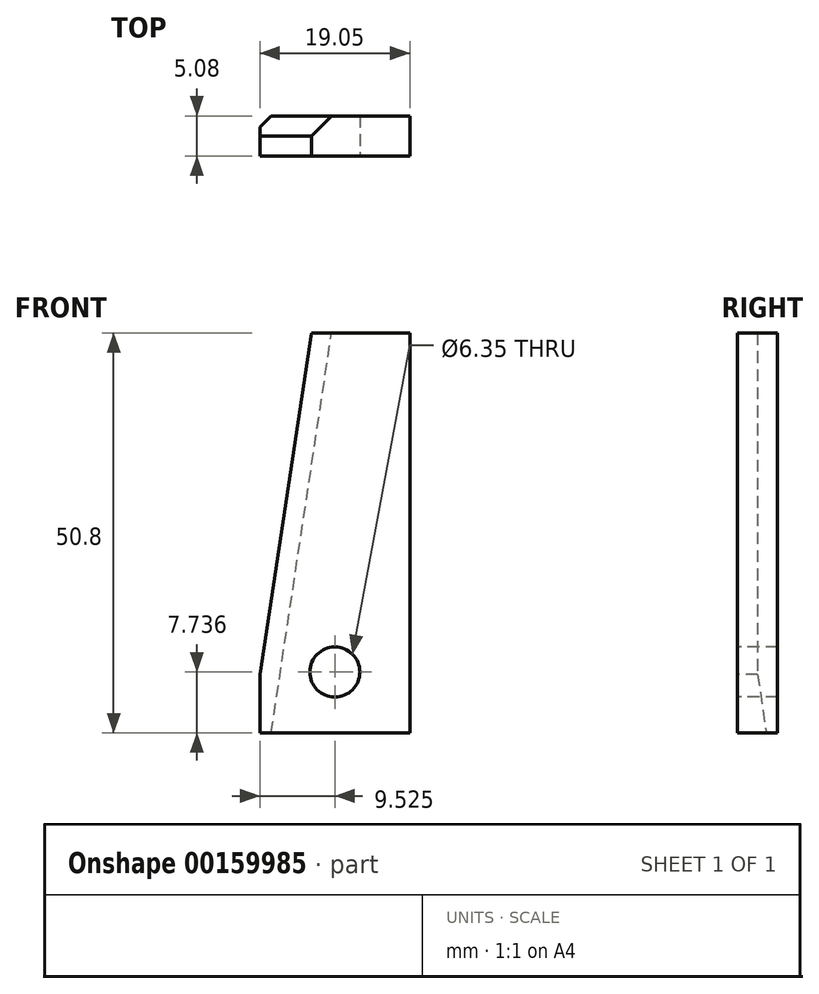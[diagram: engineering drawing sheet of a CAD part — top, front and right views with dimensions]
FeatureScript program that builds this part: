
annotation { "Feature Type Name" : "Feature", "Feature Type Description" : "" }
export const myFeature = defineFeature(function(context is Context, id is Id, definition is map)
    precondition{}
    {
        {
            var Q0;
            Q0=qCreatedBy(makeId("Front.planeOp"),FACE);
            var sketch = newSketch(context, id + "F0", { "sketchPlane" : qUnion([Q0])});
            skLineSegment(sketch, "E0.bottom", {"start": v(0, 0) * mm, "end": v(-19.05, 0) * mm});
            skLineSegment(sketch, "E0.top", {"start": v(0, 50.8) * mm, "end": v(-19.05, 50.8) * mm});
            skLineSegment(sketch, "E0.left", {"start": v(0, 0) * mm, "end": v(0, 50.8) * mm});
            skLineSegment(sketch, "E0.right", {"start": v(-19.05, 0) * mm, "end": v(-19.05, 50.8) * mm});
            skSolve(sketch);
        }
        {
            var Q0;
            Q0=makeQuery(id+"F0.imprint","IMPRINT",FACE,{"disambiguationData":[TD([[makeQuery(id+"F0.imprint","IMPRINT",EDGE,{"derivedFrom":sQuery(id+"F0.wireOp",EDGE,"E0.bottom")}),-1.0]])]});
            extrude(context, id + "F1", {"entities" : qUnion([Q0]), "depth" : 5.08 * mm});
        }
        {
            var Q0;
            Q0=makeQuery(id+"F1.opExtrude","CAP_FACE",FACE,{"disambiguationData":[OSD([sQuery(id+"F0.wireOp",EDGE,"E0.bottom"),sQuery(id+"F0.wireOp",EDGE,"E0.top"),sQuery(id+"F0.wireOp",EDGE,"E0.left"),sQuery(id+"F0.wireOp",EDGE,"E0.right")])],"isStart":false});
            var sketch = newSketch(context, id + "F2", { "sketchPlane" : qUnion([Q0])});
            skCircle(sketch, "E1", {"center": v(-9.53, 7.74) * mm, "radius": 3.18 * mm});
            skPoint(sketch, "E1.centerSnap0", {"position": v(-9.53, 0) * mm});
            skSolve(sketch);
        }
        {
            var Q0;
            Q0=sQuery(id+"F2.wireOp",VERTEX,"E1.center");
            var Q1;
            Q1=makeQuery(id+"F1.opExtrude","SWEPT_BODY",BODY,{"disambiguationData":[OSD([sQuery(id+"F0.wireOp",EDGE,"E0.bottom"),sQuery(id+"F0.wireOp",EDGE,"E0.top"),sQuery(id+"F0.wireOp",EDGE,"E0.left"),sQuery(id+"F0.wireOp",EDGE,"E0.right")])]});
            hole(context, id + "F3", {"style" : HoleStyle.SIMPLE, "endStyle" : HoleEndStyle.THROUGH, "holeDiameter" : 6.35 * mm, "locations" : qUnion([Q0]), "scope" : qUnion([Q1]), "isTappedThrough" : true});
        }
        {
            var Q0;
            Q0=makeQuery(id+"F1.opExtrude","CAP_FACE",FACE,{"disambiguationData":[OSD([sQuery(id+"F0.wireOp",EDGE,"E0.bottom"),sQuery(id+"F0.wireOp",EDGE,"E0.top"),sQuery(id+"F0.wireOp",EDGE,"E0.left"),sQuery(id+"F0.wireOp",EDGE,"E0.right")])],"isStart":false});
            var sketch = newSketch(context, id + "F4", { "sketchPlane" : qUnion([Q0])});
            skLineSegment(sketch, "E2", {"start": v(-12.41, 51.4) * mm, "end": v(-19.05, 7.46) * mm});
            skSolve(sketch);
        }
        {
            var Q0;
            {var subQ0=sQuery(id+"F4.wireOp",EDGE,"E2");var subQ1=makeQuery(id+"F1.opExtrude","CAP_EDGE",EDGE,{"disambiguationData":[OSD([sQuery(id+"F0.wireOp",EDGE,"E0.right")])],"isStart":false});var subQ2=makeQuery(id+"F4.imprint","INTERSECT",VERTEX,{"derivedFrom":[subQ1,subQ0]});Q0=makeQuery(id+"F4.imprint","IMPRINT",FACE,{"disambiguationData":[TD([[makeQuery(id+"F4.imprint","IMPRINT",EDGE,{"disambiguationData":[TD([[subQ2,1.0]])],"derivedFrom":subQ0}),-1.0]])]});}
            extrude(context, id + "F5", {"entities" : qUnion([Q0]), "operationType" : NewBodyOperationType.REMOVE, "oppositeDirection" : true, "depth" : 25.4 * mm});
        }
        {
            var Q0;
            Q0=makeQuery(id+"F5.boolean.opBoolean","COPY",EDGE,{"derivedFrom":makeQuery(id+"F5.opExtrude","CAP_EDGE",EDGE,{"disambiguationData":[OSD([sQuery(id+"F4.wireOp",EDGE,"E2")])],"isStart":true})});
            var Q1;
            Q1=makeQuery(id+"F5.boolean.opBoolean","INTERSECT",EDGE,{"derivedFrom":[makeQuery(id+"F1.opExtrude","CAP_FACE",FACE,{"disambiguationData":[OSD([sQuery(id+"F0.wireOp",EDGE,"E0.bottom"),sQuery(id+"F0.wireOp",EDGE,"E0.top"),sQuery(id+"F0.wireOp",EDGE,"E0.left"),sQuery(id+"F0.wireOp",EDGE,"E0.right")])],"isStart":true}),makeQuery(id+"F5.opExtrude","SWEPT_FACE",FACE,{"disambiguationData":[OSD([sQuery(id+"F4.wireOp",EDGE,"E2")])]})]});
            chamfer(context, id + "F6", {"entities" : qUnion([Q0, Q1]), "width" : 2.54 * mm, "tangentPropagation" : true});
        }
    });
